# Revit family: HARMANN - INDUFLOW 250
name_source: partatom
category: Mechanical Equipment
units: mm (PartAtom-declared; Revit-internal decimal feet)

## family parameters
Always vertical = No
Cut with Voids When Loaded = No
Maintain Annotation Orientation = No
OmniClass Number = 23.75.00.00
OmniClass Title = Climate Control (HVAC)
Part Type = Normal
Room Calculation Point = No
Round Connector Dimension = Use Diameter
Shared = No
Work Plane-Based = No

## types (3) — shared parameters
A = 507 mm  [stored 1.66339 ft]
Autor = https://www.archispace.com
C = 121 mm  [stored 0.396982 ft]
Description = Strumieniowy wentylator typu „jet” przeznaczony do pracy w systemach wentylacji bytowej garaży.
G = 80.5 mm  [stored 0.264108 ft]
H = 5 mm  [stored 0.0164042 ft]
Ilość faz = 1
K = 578 mm  [stored 1.89633 ft]
Lookup Table Name = INDUFLOW_ 250 EC
Manufacturer = Harmann Polska Sp. z o.o.
Model = INDUFLOW 250 EC
Obroty maksymalne nmax = 2600.000 RPM
Potencjometr = MTP 10 / MTV-010/ MTP 40
Temperatura maksymalna Tmax = 50 °C
Wyłącznik serwisowy = AS
Zasilanie Częstotliwość Nominalna = 50 Hz
Zasilanie Rodzaj Sterowania = Sterowanie napięciem 0-10V
Zasilanie napięcie nominalne Unom = 230 V
zero-valued in all types: Default Elevation

## per-type parameters (varying)
| type | B | Ciśnienie akustyczne nominalne Lpa | E | EC1 i EC2 | EC3 | F | Masa | N1 | Numer artykułu | Powietrze Przepływ Maksymalny Qmax | Siła ciągu F | Zasilanie Moc maksymalna Pmax | Zasilanie natężenie maksymalne Imax | a | b | c |
| INDUFLOW 250 EC1 | 357 mm  [stored 1.17126 ft] | 60.0 dB(A) | 383 mm  [stored 1.25656 ft] | Yes | No | 407 mm  [stored 1.3353 ft] | 6.50 kg | 1 mm | 16602800 | 980 m³/h | 6.60 N | 168 W | 1 A | 74.5 mm | 106.5 mm | 81 mm |
| INDUFLOW 250 EC2 | 702 mm  [stored 2.30315 ft] | 62.0 dB(A) | 728 mm  [stored 2.38845 ft] | Yes | No | 752 mm  [stored 2.46719 ft] | 12.30 kg | 2 mm | 16581800 | 1930 m³/h | 13.00 N | 339 W | 3 A | 106.5 mm | 96.5 mm | 95 mm |
| INDUFLOW 250 EC3 | 1053 mm  [stored 3.45472 ft] | 60.0 dB(A) | 1079 mm  [stored 3.54003 ft] | No | Yes | 1103 mm  [stored 3.61877 ft] | 18.30 kg | 3 mm | 16598500 | 3020 m³/h | 13.00 N | 502 W | 4 A | 106.5 mm | 96.5 mm | 95 mm |

note: [stored X ft] marks values corroborated as IEEE doubles in the binary element streams (Revit-internal decimal feet)

## geometry (parser evidence)
native form markers: Sweep x2
no freeform markers — native parametric forms only
